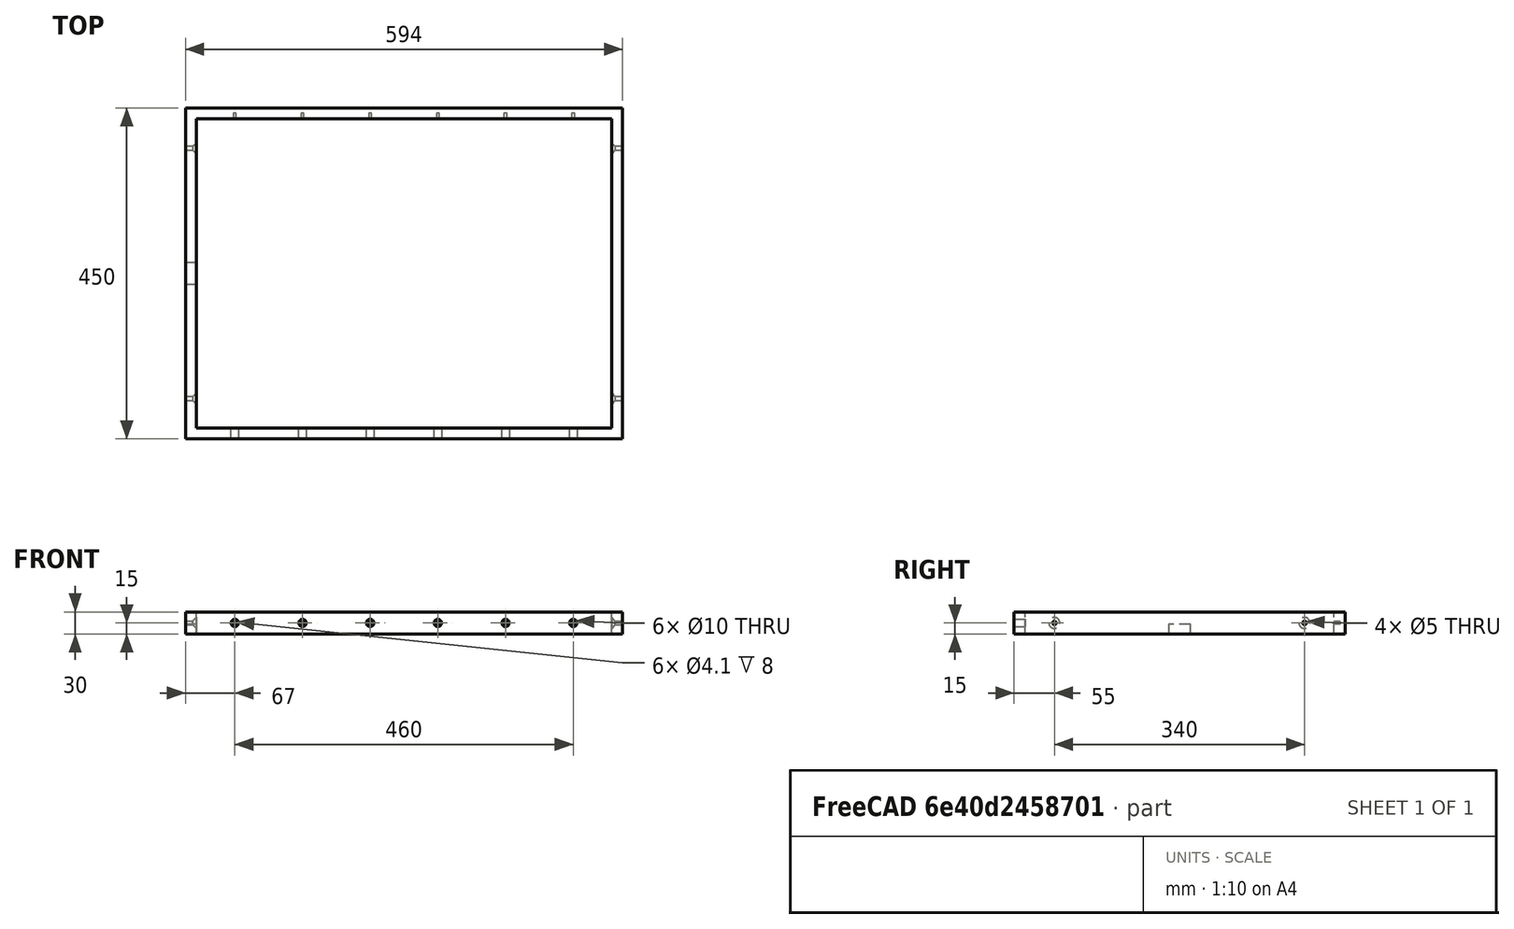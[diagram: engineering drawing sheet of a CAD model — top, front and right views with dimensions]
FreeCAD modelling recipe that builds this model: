
FCSTD DOCUMENT  (FreeCAD 1.0R39319 (Git))
Label: 02_frame_15_x_30
License: All rights reserved
LicenseURL: http://en.wikipedia.org/wiki/All_rights_reserved
objects: TechDraw::DrawViewDimension×20, TechDraw::DrawViewBalloon×9, Sketcher::SketchObject×5, TechDraw::DrawProjGroupItem×5, PartDesign::Pocket×4, TechDraw::DrawViewAnnotation×2, Spreadsheet::Sheet×1, PartDesign::Pad×1, PartDesign::Chamfer×1, PartDesign::Body×1, TechDraw::DrawSVGTemplate×1, TechDraw::DrawProjGroup×1, TechDraw::DrawPage×1
note: 59 computed .brp shape members not serialized (recipe doc carries the construction recipe); baked Part::Feature solids carry a one-line shape summary decoded from their .brp

FEATURE [Sketcher::SketchObject] Sketch
  ArcFitTolerance = 1e-06
  AttachmentSupport = -> [XY_Plane]
  FullyConstrained = true
  MakeInternals = false
  MapMode = 5
  expr: Constraints[22] = Spreadsheet.height_outside
  expr: Constraints[23] = Spreadsheet.lenght_outside
  expr: Constraints[24] = Spreadsheet.lenght_outside - 2 * Spreadsheet.height_frame
  expr: Constraints[25] = Spreadsheet.height_outside - 2 * Spreadsheet.height_frame
  sketch-geometry (10):
    g0: LineSegment StartX=-282 StartY=210 StartZ=0 EndX=-282 EndY=-210 EndZ=0
    g1: LineSegment StartX=-282 StartY=-210 StartZ=0 EndX=282 EndY=-210 EndZ=0
    g2: LineSegment StartX=282 StartY=-210 StartZ=0 EndX=282 EndY=210 EndZ=0
    g3: LineSegment StartX=282 StartY=210 StartZ=0 EndX=-282 EndY=210 EndZ=0
    g4: LineSegment [constr] StartX=-282 StartY=210 StartZ=0 EndX=282 EndY=-210 EndZ=0
    g5: LineSegment StartX=-297 StartY=225 StartZ=0 EndX=-297 EndY=-225 EndZ=0
    g6: LineSegment StartX=-297 StartY=-225 StartZ=0 EndX=297 EndY=-225 EndZ=0
    g7: LineSegment StartX=297 StartY=-225 StartZ=0 EndX=297 EndY=225 EndZ=0
    g8: LineSegment StartX=297 StartY=225 StartZ=0 EndX=-297 EndY=225 EndZ=0
    g9: LineSegment [constr] StartX=-297 StartY=225 StartZ=0 EndX=297 EndY=-225 EndZ=0
  constraints (26):
    c: Coincident(g0,g1)
    c: Coincident(g1,g2)
    c: Coincident(g2,g3)
    c: Coincident(g3,g0)
    c: Vertical(g0)
    c: Vertical(g2)
    c: Horizontal(g1)
    c: Horizontal(g3)
    c: Coincident(g4,g0)
    c: Coincident(g4,g1)
    c: Symmetric(g0,g1,g-1)
    c: Coincident(g5,g6)
    c: Coincident(g6,g7)
    c: Coincident(g7,g8)
    c: Coincident(g8,g5)
    c: Vertical(g5)
    c: Vertical(g7)
    c: Horizontal(g6)
    c: Horizontal(g8)
    c: Coincident(g9,g5)
    c: Coincident(g9,g6)
    c: Symmetric(g5,g6,g-1)
    c: DistanceY(g5,g5) = 450
    c: DistanceX(g8,g8) = 594
    c: DistanceX(g3,g3) = 564
    c: DistanceY(g0,g0) = 420
FEATURE [Spreadsheet::Sheet] Spreadsheet
  cells = A2='lenght_outside; B2(lenght_outside)=594; A3='height_outside; B3(height_outside)=450; A5='width_frame; B5(width_frame)=30; A6='height_frame; B6(height_frame)=15; A7='drill_size; B7(drillsize)=81
FEATURE [PartDesign::Pad] Pad
  Direction = (0,0,1)
  Length = 30
  Length2 = 10
  Profile = -> Sketch
  ReferenceAxis = -> Sketch [N_Axis]
  Suppressed = false
  Type = 0
  expr: Length = Spreadsheet.width_frame
FEATURE [Sketcher::SketchObject] Sketch001
  ArcFitTolerance = 1e-06
  AttachmentSupport = -> [YZ_Plane]
  FullyConstrained = true
  MakeInternals = false
  MapMode = 5
  Placement = pos=(0,0,0) rot=(0.57735,0.57735,0.57735;2.0944rad)
  sketch-geometry (4):
    g0: LineSegment StartX=-15 StartY=13 StartZ=0 EndX=-15 EndY=0 EndZ=0
    g1: LineSegment StartX=-15 StartY=0 StartZ=0 EndX=15 EndY=0 EndZ=0
    g2: LineSegment StartX=15 StartY=0 StartZ=0 EndX=15 EndY=13 EndZ=0
    g3: LineSegment StartX=15 StartY=13 StartZ=0 EndX=-15 EndY=13 EndZ=0
  constraints (11):
    c: Coincident(g0,g1)
    c: Coincident(g1,g2)
    c: Coincident(g2,g3)
    c: Coincident(g3,g0)
    c: Vertical(g0)
    c: Vertical(g2)
    c: Horizontal(g1)
    c: Symmetric(g0,g2,g-2)
    c: Horizontal(g1,g-1)
    c: DistanceX(g3,g3) = 30
    c: DistanceY(g0,g0) = 13
FEATURE [PartDesign::Pocket] Pocket
  BaseFeature = -> Pad
  Direction = (-1,0,0)
  Length = 594
  Length2 = 5
  Profile = -> Sketch001
  ReferenceAxis = -> Sketch001 [N_Axis]
  Suppressed = false
  Type = 0
  expr: Length = Spreadsheet.lenght_outside
FEATURE [Sketcher::SketchObject] Sketch002
  ArcFitTolerance = 1e-06
  AttachmentSupport = -> [XZ_Plane]
  ExternalGeometry = -> [Pocket]
  FullyConstrained = true
  MakeInternals = false
  MapMode = 5
  Placement = pos=(0,0,0) rot=(1,0,0;1.5708rad)
  sketch-geometry (7):
    g0: LineSegment [constr] StartX=-282 StartY=15 StartZ=0 EndX=282 EndY=15 EndZ=0
    g1: Circle CenterX=-230 CenterY=15 CenterZ=0 NormalX=0 NormalY=0 NormalZ=1 AngleXU=0 Radius=5
    g2: Circle CenterX=-138 CenterY=15 CenterZ=0 NormalX=0 NormalY=0 NormalZ=1 AngleXU=0 Radius=5
    g3: Circle CenterX=-46 CenterY=15 CenterZ=0 NormalX=0 NormalY=0 NormalZ=1 AngleXU=0 Radius=5
    g4: Circle CenterX=46 CenterY=15 CenterZ=0 NormalX=0 NormalY=0 NormalZ=1 AngleXU=0 Radius=5
    g5: Circle CenterX=138 CenterY=15 CenterZ=0 NormalX=0 NormalY=0 NormalZ=1 AngleXU=0 Radius=5
    g6: Circle CenterX=230 CenterY=15 CenterZ=0 NormalX=0 NormalY=0 NormalZ=1 AngleXU=0 Radius=5
  constraints (23):
    c: Symmetric(g-5,g-5,g0)
    c: Symmetric(g-6,g-6,g0)
    c: DistanceX(g-3,g-3) = 564
    c: PointOnObject(g1,g0)
    c: Diameter(g1) = 10
    c: PointOnObject(g2,g0)
    c: PointOnObject(g3,g0)
    c: PointOnObject(g4,g0)
    c: PointOnObject(g5,g0)
    c: Equal(g1,g2)
    c: Equal(g1,g3)
    c: Equal(g1,g4)
    c: Equal(g5,g1)
    c: PointOnObject(g6,g0)
    c: Equal(g1,g6)
    c: DistanceX(g0,g1) = 52
    c: DistanceX(g6,g0) = 52
    c: DistanceX(g1,g6) = 460
    c: DistanceX(g1,g2) = 92
    c: DistanceX(g2,g3) = 92
    c: DistanceX(g3,g4) = 92
    c: DistanceX(g4,g5) = 92
    c: DistanceX(g5,g6) = 92
FEATURE [PartDesign::Pocket] Pocket001
  BaseFeature = -> Pocket
  Direction = (0,1,-2e-16)
  Length = 225
  Length2 = 5
  Profile = -> Sketch002
  ReferenceAxis = -> Sketch002 [N_Axis]
  Reversed = true
  Suppressed = false
  Type = 0
  expr: Length = Spreadsheet.height_outside / 2
FEATURE [Sketcher::SketchObject] Sketch003
  ArcFitTolerance = 1e-06
  AttachmentSupport = -> [XZ_Plane]
  ExternalGeometry = -> [Pocket001]
  FullyConstrained = true
  MakeInternals = false
  MapMode = 5
  Placement = pos=(0,0,0) rot=(1,0,0;1.5708rad)
  sketch-geometry (7):
    g0: LineSegment [constr] StartX=-282 StartY=15 StartZ=0 EndX=282 EndY=15 EndZ=0
    g1: Circle CenterX=-230 CenterY=15 CenterZ=0 NormalX=0 NormalY=0 NormalZ=1 AngleXU=0 Radius=2.05
    g2: Circle CenterX=-138 CenterY=15 CenterZ=0 NormalX=0 NormalY=0 NormalZ=1 AngleXU=0 Radius=2.05
    g3: Circle CenterX=-46 CenterY=15 CenterZ=0 NormalX=0 NormalY=0 NormalZ=1 AngleXU=0 Radius=2.05
    g4: Circle CenterX=46 CenterY=15 CenterZ=0 NormalX=0 NormalY=0 NormalZ=1 AngleXU=0 Radius=2.05
    g5: Circle CenterX=138 CenterY=15 CenterZ=0 NormalX=0 NormalY=0 NormalZ=1 AngleXU=0 Radius=2.05
    g6: Circle CenterX=230 CenterY=15 CenterZ=0 NormalX=0 NormalY=0 NormalZ=1 AngleXU=0 Radius=2.05
  constraints (22):
    c: Horizontal(g0)
    c: PointOnObject(g0,g-4)
    c: Symmetric(g-3,g-3,g0)
    c: PointOnObject(g1,g0)
    c: Distance(g1,g-3) = 52
    c: Diameter(g1) = 4.1
    c: PointOnObject(g2,g0)
    c: DistanceX(g1,g2) = 92
    c: Equal(g1,g2)
    c: PointOnObject(g3,g0)
    c: Equal(g2,g3)
    c: PointOnObject(g4,g0)
    c: PointOnObject(g5,g0)
    c: Equal(g1,g4)
    c: Equal(g1,g5)
    c: DistanceX(g2,g3) = 92
    c: DistanceX(g3,g4) = 92
    c: DistanceX(g4,g5) = 92
    c: PointOnObject(g6,g0)
    c: Equal(g1,g6)
    c: DistanceX(g5,g6) = 92
    c: DistanceX(g6,g0) = 52
FEATURE [PartDesign::Pocket] Pocket002
  BaseFeature = -> Pocket001
  Direction = (0,1,-2e-16)
  Length = 218
  Length2 = 5
  Profile = -> Sketch003
  ReferenceAxis = -> Sketch003 [N_Axis]
  Suppressed = false
  Type = 0
  expr: Length = Spreadsheet.height_outside / 2 - 7
FEATURE [Sketcher::SketchObject] Sketch004
  ArcFitTolerance = 1e-06
  AttachmentSupport = -> [YZ_Plane]
  ExternalGeometry = -> [Pocket002]
  FullyConstrained = true
  MakeInternals = false
  MapMode = 5
  Placement = pos=(0,0,0) rot=(0.57735,0.57735,0.57735;2.0944rad)
  sketch-geometry (3):
    g0: LineSegment [constr] StartX=-210 StartY=15 StartZ=0 EndX=210 EndY=15 EndZ=0
    g1: Circle CenterX=-170 CenterY=15 CenterZ=0 NormalX=0 NormalY=0 NormalZ=1 AngleXU=0 Radius=2.5
    g2: Circle CenterX=170 CenterY=15 CenterZ=0 NormalX=0 NormalY=0 NormalZ=1 AngleXU=0 Radius=2.5
  constraints (8):
    c: Symmetric(g-3,g-3,g0)
    c: Symmetric(g-4,g-4,g0)
    c: PointOnObject(g1,g0)
    c: PointOnObject(g2,g0)
    c: Distance(g1,g-3) = 40
    c: Distance(g0,g2) = 40
    c: Diameter(g1) = 5
    c: Equal(g1,g2)
FEATURE [PartDesign::Pocket] Pocket003
  BaseFeature = -> Pocket002
  Direction = (-1,0,0)
  Length = 5
  Length2 = 5
  Midplane = true
  Profile = -> Sketch004
  ReferenceAxis = -> Sketch004 [N_Axis]
  Suppressed = false
  Type = 1
FEATURE [PartDesign::Chamfer] Chamfer
  Angle = 45
  Base = -> Pocket003 [Edge41,Edge43,Edge57,Edge58]
  BaseFeature = -> Pocket003
  ChamferType = 0
  FlipDirection = false
  Size = 5
  Size2 = 1
  SupportTransform = false
  Suppressed = false
  UseAllEdges = false
FEATURE [PartDesign::Body] Body
  AllowCompound = false
  Group = -> [Sketch,Pad,Sketch001,Pocket,Sketch002,Pocket001,Sketch003,Pocket002,Sketch004,Pocket003,Chamfer]
  Origin = -> Origin
  Tip = -> Chamfer
FEATURE [TechDraw::DrawSVGTemplate] Template
  EditableTexts = AuthorName=Matthias Mosimann; CheckDate=N/A; CreationDate=15/04/2026; DrawingNumber=1.0; FC-Title=Rahmen; SheetNumber=1 / 1; SupervisorName=N/A; Weight=WEIGHT; scale=1 : 5
  Height = 297
  Orientation = 1
  Template = C:/Program Files/FreeCAD 1.0/data/Mod/TechDraw/Templates/A3_Landscape_TD.svg
  Width = 420
FEATURE [TechDraw::DrawProjGroupItem] View  label="Front"
  CoarseView = false
  Direction = (0,-1,0)
  Focus = 100
  HardHidden = false
  IsoCount = 0
  IsoHidden = false
  IsoVisible = false
  LockPosition = true
  Perspective = false
  Rotation = 0
  RotationVector = (1,0,0)
  Scale = 0.2
  ScaleType = 2
  ScrubCount = 1
  SeamHidden = false
  SeamVisible = true
  SmoothHidden = false
  SmoothVisible = true
  Source = -> [Body]
  Type = 0
  X = 0
  XDirection = (-1,0,-1e-16)
  Y = 0
FEATURE [TechDraw::DrawProjGroupItem] ProjItem  label="Right"
  CoarseView = false
  Direction = (-1,-1e-16,-1e-16)
  Focus = 100
  HardHidden = false
  IsoCount = 0
  IsoHidden = false
  IsoVisible = false
  LockPosition = true
  Perspective = false
  Rotation = 0
  RotationVector = (1,0,0)
  Scale = 0.2
  ScaleType = 2
  ScrubCount = 1
  SeamHidden = false
  SeamVisible = true
  SmoothHidden = false
  SmoothVisible = true
  Source = -> [Body]
  Type = 2
  X = -119.062
  XDirection = (-1e-16,1,0)
  Y = 0
FEATURE [TechDraw::DrawProjGroupItem] ProjItem002  label="Top"
  CoarseView = false
  Direction = (1e-16,0,-1)
  Focus = 100
  HardHidden = true
  IsoCount = 0
  IsoHidden = false
  IsoVisible = false
  LockPosition = true
  Perspective = false
  Rotation = 0
  RotationVector = (1,0,0)
  Scale = 0.2
  ScaleType = 2
  ScrubCount = 1
  SeamHidden = false
  SeamVisible = true
  SmoothHidden = false
  SmoothVisible = true
  Source = -> [Body]
  Type = 4
  X = 0
  XDirection = (-1,0,-1e-16)
  Y = -80.6268
FEATURE [TechDraw::DrawProjGroupItem] ProjItem003  label="Left"
  CoarseView = false
  Direction = (1,-1e-16,1e-16)
  Focus = 100
  HardHidden = false
  IsoCount = 0
  IsoHidden = false
  IsoVisible = false
  LockPosition = true
  Perspective = false
  Rotation = 0
  RotationVector = (1,0,0)
  Scale = 0.2
  ScaleType = 2
  ScrubCount = 1
  SeamHidden = false
  SeamVisible = true
  SmoothHidden = false
  SmoothVisible = true
  Source = -> [Body]
  Type = 1
  X = 121.888
  XDirection = (-1e-16,-1,0)
  Y = 0
FEATURE [TechDraw::DrawProjGroupItem] ProjItem004  label="FrontTopLeft"
  CoarseView = false
  Direction = (0.57735,-0.57735,-0.57735)
  Focus = 100
  HardHidden = false
  IsoCount = 0
  IsoHidden = false
  IsoVisible = false
  LockPosition = true
  Perspective = false
  Rotation = 0
  RotationVector = (1,0,0)
  Scale = 0.2
  ScaleType = 2
  ScrubCount = 1
  SeamHidden = false
  SeamVisible = true
  SmoothHidden = false
  SmoothVisible = true
  Source = -> [Body]
  Type = 6
  X = 147.596
  XDirection = (-0.707107,-0.707107,-1e-16)
  Y = -76.8368
FEATURE [TechDraw::DrawProjGroup] ProjGroup
  Anchor = -> View
  AutoDistribute = true
  LockPosition = false
  ProjectionType = 0
  Rotation = 0
  Scale = 0.2
  ScaleType = 2
  Source = -> [Body]
  Views = -> [View,ProjItem,ProjItem002,ProjItem003,ProjItem004]
  X = 185.522
  Y = 222.445
  spacingX = 15
  spacingY = 15
FEATURE [TechDraw::DrawViewDimension] Dimension
  AngleOverride = false
  Arbitrary = false
  ArbitraryTolerances = false
  BoxCorners = (2) [(-59.4,-45,0),(59.4,45,0)]
  EqualTolerance = true
  ExtensionAngle = 0
  FormatSpec = %.2w
  FormatSpecOverTolerance = %+.2w
  FormatSpecUnderTolerance = %+.2w
  Inverted = false
  LineAngle = 0
  LockPosition = false
  MeasureType = 1
  OverTolerance = 0
  References2D = -> [ProjItem002]
  Rotation = 0
  ScaleType = 0
  TheoreticalExact = false
  Type = 2
  UnderTolerance = 0
  X = -72.114
  Y = 5.93997
FEATURE [TechDraw::DrawViewDimension] Dimension001
  AngleOverride = false
  Arbitrary = false
  ArbitraryTolerances = false
  BoxCorners = (2) [(-59.4,-45,0),(59.4,45,0)]
  EqualTolerance = true
  ExtensionAngle = 0
  FormatSpec = %.2w
  FormatSpecOverTolerance = %+.2w
  FormatSpecUnderTolerance = %+.2w
  Inverted = false
  LineAngle = 0
  LockPosition = false
  MeasureType = 1
  OverTolerance = 0
  References2D = -> [ProjItem002]
  Rotation = 0
  ScaleType = 0
  TheoreticalExact = false
  Type = 1
  UnderTolerance = 0
  X = 0
  Y = 61.892
FEATURE [TechDraw::DrawViewDimension] Dimension002
  AngleOverride = false
  Arbitrary = false
  ArbitraryTolerances = false
  BoxCorners = (2) [(-45,-3,0),(45,3,0)]
  EqualTolerance = true
  ExtensionAngle = 0
  FormatSpec = %.2w
  FormatSpecOverTolerance = %+.2w
  FormatSpecUnderTolerance = %+.2w
  Inverted = false
  LineAngle = 0
  LockPosition = false
  MeasureType = 1
  OverTolerance = 0
  References2D = -> [ProjItem]
  Rotation = 0
  ScaleType = 0
  TheoreticalExact = false
  Type = 0
  UnderTolerance = 0
  X = -39.5
  Y = -15.8335
FEATURE [TechDraw::DrawViewDimension] Dimension003
  AngleOverride = false
  Arbitrary = false
  ArbitraryTolerances = false
  BoxCorners = (2) [(-45,-3,0),(45,3,0)]
  EqualTolerance = true
  ExtensionAngle = 0
  FormatSpec = ⌀%.2w
  FormatSpecOverTolerance = %+.2w
  FormatSpecUnderTolerance = %+.2w
  Inverted = false
  LineAngle = 0
  LockPosition = false
  MeasureType = 1
  OverTolerance = 0
  References2D = -> [ProjItem]
  Rotation = 0
  ScaleType = 0
  TheoreticalExact = false
  Type = 5
  UnderTolerance = 0
  X = -30.7122
  Y = 14.8466
FEATURE [TechDraw::DrawViewDimension] Dimension004
  AngleOverride = false
  Arbitrary = false
  ArbitraryTolerances = false
  BoxCorners = (2) [(-45,-3,0),(45,3,0)]
  EqualTolerance = true
  ExtensionAngle = 0
  FormatSpec = %.2w
  FormatSpecOverTolerance = %+.2w
  FormatSpecUnderTolerance = %+.2w
  Inverted = false
  LineAngle = 0
  LockPosition = false
  MeasureType = 1
  OverTolerance = 0
  References2D = -> [ProjItem]
  Rotation = 0
  ScaleType = 0
  TheoreticalExact = false
  Type = 0
  UnderTolerance = 0
  X = 39.5
  Y = -15.8335
FEATURE [TechDraw::DrawViewDimension] Dimension005
  AngleOverride = false
  Arbitrary = false
  ArbitraryTolerances = false
  BoxCorners = (2) [(-45,-3,0),(45,3,0)]
  EqualTolerance = true
  ExtensionAngle = 0
  FormatSpec = ⌀%.2w
  FormatSpecOverTolerance = %+.2w
  FormatSpecUnderTolerance = %+.2w
  Inverted = false
  LineAngle = 0
  LockPosition = false
  MeasureType = 1
  OverTolerance = 0
  References2D = -> [ProjItem]
  Rotation = 0
  ScaleType = 0
  TheoreticalExact = false
  Type = 5
  UnderTolerance = 0
  X = 38.1595
  Y = 15.5364
FEATURE [TechDraw::DrawViewDimension] Dimension006
  AngleOverride = false
  Arbitrary = false
  ArbitraryTolerances = false
  BoxCorners = (2) [(-45,-3,0),(45,3,0)]
  EqualTolerance = true
  ExtensionAngle = 0
  FormatSpec = %.2w
  FormatSpecOverTolerance = %+.2w
  FormatSpecUnderTolerance = %+.2w
  Inverted = false
  LineAngle = 0
  LockPosition = false
  MeasureType = 1
  OverTolerance = 0
  References2D = -> [ProjItem]
  Rotation = 0
  ScaleType = 0
  TheoreticalExact = false
  Type = 0
  UnderTolerance = 0
  X = -13.9563
  Y = 10.1442
FEATURE [TechDraw::DrawViewDimension] Dimension007
  AngleOverride = false
  Arbitrary = false
  ArbitraryTolerances = false
  BoxCorners = (2) [(-45,-3,0),(45,3,0)]
  EqualTolerance = true
  ExtensionAngle = 0
  FormatSpec = %.2w
  FormatSpecOverTolerance = %+.2w
  FormatSpecUnderTolerance = %+.2w
  Inverted = false
  LineAngle = 0
  LockPosition = false
  MeasureType = 1
  OverTolerance = 0
  References2D = -> [ProjItem]
  Rotation = 0
  ScaleType = 0
  TheoreticalExact = false
  Type = 0
  UnderTolerance = 0
  X = -17.7771
  Y = 24.7768
FEATURE [TechDraw::DrawViewDimension] Dimension008
  AngleOverride = false
  Arbitrary = false
  ArbitraryTolerances = false
  BoxCorners = (2) [(-59.4,-3,0),(59.4,3,0)]
  EqualTolerance = true
  ExtensionAngle = 0
  FormatSpec = %.2w
  FormatSpecOverTolerance = %+.2w
  FormatSpecUnderTolerance = %+.2w
  Inverted = false
  LineAngle = 0
  LockPosition = false
  MeasureType = 1
  OverTolerance = 0
  References2D = -> [View]
  Rotation = 0
  ScaleType = 0
  TheoreticalExact = false
  Type = 0
  UnderTolerance = 0
  X = -52.7
  Y = 22.4873
FEATURE [TechDraw::DrawViewDimension] Dimension009
  AngleOverride = false
  Arbitrary = false
  ArbitraryTolerances = false
  BoxCorners = (2) [(-59.4,-3,0),(59.4,3,0)]
  EqualTolerance = true
  ExtensionAngle = 0
  FormatSpec = %.2w
  FormatSpecOverTolerance = %+.2w
  FormatSpecUnderTolerance = %+.2w
  Inverted = false
  LineAngle = 0
  LockPosition = false
  MeasureType = 1
  OverTolerance = 0
  References2D = -> [View]
  Rotation = 0
  ScaleType = 0
  TheoreticalExact = false
  Type = 1
  UnderTolerance = 0
  X = -36.8
  Y = 22.4873
FEATURE [TechDraw::DrawViewDimension] Dimension010
  AngleOverride = false
  Arbitrary = false
  ArbitraryTolerances = false
  BoxCorners = (2) [(-59.4,-3,0),(59.4,3,0)]
  EqualTolerance = true
  ExtensionAngle = 0
  FormatSpec = %.2w
  FormatSpecOverTolerance = %+.2w
  FormatSpecUnderTolerance = %+.2w
  Inverted = false
  LineAngle = 0
  LockPosition = false
  MeasureType = 1
  OverTolerance = 0
  References2D = -> [View]
  Rotation = 0
  ScaleType = 0
  TheoreticalExact = false
  Type = 2
  UnderTolerance = 0
  X = 65.2162
  Y = 0
FEATURE [TechDraw::DrawViewDimension] Dimension011
  AngleOverride = false
  Arbitrary = false
  ArbitraryTolerances = false
  BoxCorners = (2) [(-59.4,-45,0),(59.4,45,0)]
  EqualTolerance = true
  ExtensionAngle = 0
  FormatSpec = %.2w
  FormatSpecOverTolerance = %+.2w
  FormatSpecUnderTolerance = %+.2w
  Inverted = false
  LineAngle = 0
  LockPosition = false
  MeasureType = 1
  OverTolerance = 0
  References2D = -> [ProjItem002]
  Rotation = 0
  ScaleType = 0
  TheoreticalExact = false
  Type = 0
  UnderTolerance = 0
  X = 62.2692
  Y = 54.4773
FEATURE [TechDraw::DrawViewDimension] Dimension012
  AngleOverride = false
  Arbitrary = false
  ArbitraryTolerances = false
  BoxCorners = (2) [(-59.4,-3,0),(59.4,3,0)]
  EqualTolerance = true
  ExtensionAngle = 0
  FormatSpec = %.2w
  FormatSpecOverTolerance = %+.2w
  FormatSpecUnderTolerance = %+.2w
  Inverted = false
  LineAngle = 0
  LockPosition = false
  MeasureType = 1
  OverTolerance = 0
  References2D = -> [View]
  Rotation = 0
  ScaleType = 0
  TheoreticalExact = false
  Type = 1
  UnderTolerance = 0
  X = -18.4
  Y = 22.4873
FEATURE [TechDraw::DrawViewDimension] Dimension013
  AngleOverride = false
  Arbitrary = false
  ArbitraryTolerances = false
  BoxCorners = (2) [(-59.4,-3,0),(59.4,3,0)]
  EqualTolerance = true
  ExtensionAngle = 0
  FormatSpec = %.2w
  FormatSpecOverTolerance = %+.2w
  FormatSpecUnderTolerance = %+.2w
  Inverted = false
  LineAngle = 0
  LockPosition = false
  MeasureType = 1
  OverTolerance = 0
  References2D = -> [View]
  Rotation = 0
  ScaleType = 0
  TheoreticalExact = false
  Type = 1
  UnderTolerance = 0
  X = 0
  Y = 22.4873
FEATURE [TechDraw::DrawViewDimension] Dimension014
  AngleOverride = false
  Arbitrary = false
  ArbitraryTolerances = false
  BoxCorners = (2) [(-59.4,-3,0),(59.4,3,0)]
  EqualTolerance = true
  ExtensionAngle = 0
  FormatSpec = %.2w
  FormatSpecOverTolerance = %+.2w
  FormatSpecUnderTolerance = %+.2w
  Inverted = false
  LineAngle = 0
  LockPosition = false
  MeasureType = 1
  OverTolerance = 0
  References2D = -> [View]
  Rotation = 0
  ScaleType = 0
  TheoreticalExact = false
  Type = 1
  UnderTolerance = 0
  X = 18.4
  Y = 22.4873
FEATURE [TechDraw::DrawViewDimension] Dimension015
  AngleOverride = false
  Arbitrary = false
  ArbitraryTolerances = false
  BoxCorners = (2) [(-59.4,-3,0),(59.4,3,0)]
  EqualTolerance = true
  ExtensionAngle = 0
  FormatSpec = %.2w
  FormatSpecOverTolerance = %+.2w
  FormatSpecUnderTolerance = %+.2w
  Inverted = false
  LineAngle = 0
  LockPosition = false
  MeasureType = 1
  OverTolerance = 0
  References2D = -> [View]
  Rotation = 0
  ScaleType = 0
  TheoreticalExact = false
  Type = 1
  UnderTolerance = 0
  X = 36.8
  Y = 22.4873
FEATURE [TechDraw::DrawViewDimension] Dimension016
  AngleOverride = false
  Arbitrary = false
  ArbitraryTolerances = false
  BoxCorners = (2) [(-59.4,-3,0),(59.4,3,0)]
  EqualTolerance = true
  ExtensionAngle = 0
  FormatSpec = %.2w
  FormatSpecOverTolerance = %+.2w
  FormatSpecUnderTolerance = %+.2w
  Inverted = false
  LineAngle = 0
  LockPosition = false
  MeasureType = 1
  OverTolerance = 0
  References2D = -> [View]
  Rotation = 0
  ScaleType = 0
  TheoreticalExact = false
  Type = 0
  UnderTolerance = 0
  X = 52.7
  Y = 22.4873
FEATURE [TechDraw::DrawViewAnnotation] Annotation005
  Font = osifont
  LineSpace = 80
  LockPosition = false
  MaxWidth = 100
  Rotation = 0
  Scale = 0.5
  ScaleType = 1
  Text = Rahmen ist aus Flachstahl 30mm x 15mm. | 3D Ansichten können von der angegebenen Skalierungsgrösse abweichen. | Alle Angaben in mm.
  TextSize = 3
  TextStyle = 1
  X = 65.8486
  Y = 170.219
FEATURE [TechDraw::DrawViewBalloon] Balloon
  BubbleShape = 0
  EndType = 0
  EndTypeScale = 1
  KinkLength = 5
  LockPosition = false
  OriginX = -67.1399
  OriginY = 96.7687
  Rotation = 0
  ScaleType = 0
  ShapeScale = 1
  SourceView = -> Annotation005
  Text = 1
  TextWrapLen = -1
  X = -98.1022
  Y = 165.989
FEATURE [TechDraw::DrawViewAnnotation] Annotation
  Font = osifont
  LineSpace = 80
  LockPosition = false
  MaxWidth = 100
  Rotation = 0
  Scale = 0.5
  ScaleType = 1
  Text = (1) Montageloch kann frei gewählt werden im Durchmesser und Platzierung. Wichtig ist dass auf der Innenseite Senkungen passend vorhanden sind. Hier sind nur Beispiele eingezeichnet.   | (2) Unten im Rahmen werden die Edelstahlhülsen mit Sackloch eingeschweist. Bohrung muss ggf. etwas grösser sein als 10mm, damit die Hülse passt. | (3) Oben im Rahmen werden nur die 4.1mm Sacklöcher gebohrt. Ohne Hülsen.
  TextSize = 3
  TextStyle = 0
  X = 65.8486
  Y = 113.793
FEATURE [TechDraw::DrawViewBalloon] Balloon002
  BubbleShape = 0
  EndType = 0
  EndTypeScale = 1
  KinkLength = 5
  LockPosition = false
  OriginX = -225
  OriginY = 0
  Rotation = 0
  ScaleType = 0
  ShapeScale = 1
  SourceView = -> View
  Text = 2
  TextWrapLen = -1
  X = -121.803
  Y = -73.4565
FEATURE [TechDraw::DrawViewBalloon] Balloon003
  BubbleShape = 0
  EndType = 0
  EndTypeScale = 1
  KinkLength = 5
  LockPosition = false
  OriginX = -5.29303
  OriginY = -183.225
  Rotation = 0
  ScaleType = 0
  ShapeScale = 1
  SourceView = -> ProjItem004
  Text = 2
  TextWrapLen = -1
  X = 166.509
  Y = -226.829
FEATURE [TechDraw::DrawViewBalloon] Balloon004
  BubbleShape = 0
  EndType = 0
  EndTypeScale = 1
  KinkLength = 5
  LockPosition = false
  OriginX = -135.95
  OriginY = 0
  Rotation = 0
  ScaleType = 0
  ShapeScale = 1
  SourceView = -> View
  Text = 3
  TextWrapLen = -1
  X = -243.989
  Y = 155.417
FEATURE [TechDraw::DrawViewBalloon] Balloon005
  BubbleShape = 0
  EndType = 0
  EndTypeScale = 1
  KinkLength = 5
  LockPosition = false
  OriginX = -116.686
  OriginY = 105.548
  Rotation = 0
  ScaleType = 0
  ShapeScale = 1
  SourceView = -> ProjItem004
  Text = 3
  TextWrapLen = -1
  X = -266.453
  Y = 203.449
FEATURE [TechDraw::DrawViewBalloon] Balloon006
  BubbleShape = 0
  EndType = 0
  EndTypeScale = 1
  KinkLength = 5
  LockPosition = false
  OriginX = 75.446
  OriginY = 191.023
  Rotation = 0
  ScaleType = 0
  ShapeScale = 1
  SourceView = -> ProjItem004
  Text = 1
  TextWrapLen = -1
  X = 175.446
  Y = 291.023
FEATURE [TechDraw::DrawViewDimension] Dimension017
  AngleOverride = false
  Arbitrary = false
  ArbitraryTolerances = false
  BoxCorners = (2) [(-59.4,-3,0),(59.4,3,0)]
  EqualTolerance = true
  ExtensionAngle = 0
  FormatSpec = ⌀%.2w
  FormatSpecOverTolerance = %+.2w
  FormatSpecUnderTolerance = %+.2w
  Inverted = false
  LineAngle = 0
  LockPosition = false
  MeasureType = 1
  OverTolerance = 0
  References2D = -> [View]
  Rotation = 0
  ScaleType = 0
  TheoreticalExact = true
  Type = 5
  UnderTolerance = 0
  X = -66.349
  Y = -6.38909
FEATURE [TechDraw::DrawViewDimension] Dimension018
  AngleOverride = false
  Arbitrary = false
  ArbitraryTolerances = false
  BoxCorners = (2) [(-59.4,-3,0),(59.4,3,0)]
  EqualTolerance = true
  ExtensionAngle = 0
  FormatSpec = ⌀%.2w
  FormatSpecOverTolerance = %+.2w
  FormatSpecUnderTolerance = %+.2w
  Inverted = false
  LineAngle = 0
  LockPosition = false
  MeasureType = 1
  OverTolerance = 0
  References2D = -> [View]
  Rotation = 0
  ScaleType = 0
  TheoreticalExact = false
  Type = 5
  UnderTolerance = 0
  X = -66.044
  Y = 23.5898
FEATURE [TechDraw::DrawViewDimension] Dimension019
  AngleOverride = false
  Arbitrary = false
  ArbitraryTolerances = false
  BoxCorners = (2) [(-59.4,-45,-1e-07),(59.4,45,1e-07)]
  EqualTolerance = true
  ExtensionAngle = 0
  FormatSpec = %.2w
  FormatSpecOverTolerance = %+.2w
  FormatSpecUnderTolerance = %+.2w
  Inverted = false
  LineAngle = 0
  LockPosition = false
  MeasureType = 1
  OverTolerance = 0
  References2D = -> [ProjItem002]
  Rotation = 0
  ScaleType = 0
  TheoreticalExact = false
  Type = 0
  UnderTolerance = 0
  X = -42.8631
  Y = 50.9888
FEATURE [TechDraw::DrawViewBalloon] Balloon007
  BubbleShape = 0
  EndType = 0
  EndTypeScale = 1
  KinkLength = 5
  LockPosition = false
  OriginX = -232.05
  OriginY = 214
  Rotation = 0
  ScaleType = 0
  ShapeScale = 1
  SourceView = -> ProjItem002
  Text = 3
  TextWrapLen = -1
  X = -331.685
  Y = 266.2
FEATURE [TechDraw::DrawViewBalloon] Balloon008
  BubbleShape = 0
  EndType = 0
  EndTypeScale = 1
  KinkLength = 5
  LockPosition = false
  OriginX = -284.5
  OriginY = 175
  Rotation = 0
  ScaleType = 0
  ShapeScale = 1
  SourceView = -> ProjItem002
  Text = 1
  TextWrapLen = -1
  X = -390.448
  Y = 196.452
FEATURE [TechDraw::DrawViewBalloon] Balloon009
  BubbleShape = 0
  EndType = 0
  EndTypeScale = 1
  KinkLength = 5
  LockPosition = false
  OriginX = -143
  OriginY = -217.5
  Rotation = 0
  ScaleType = 0
  ShapeScale = 1
  SourceView = -> ProjItem002
  Text = 2
  TextWrapLen = -1
  X = -270.817
  Y = -305.468
FEATURE [TechDraw::DrawPage] Page
  KeepUpdated = true
  NextBalloonIndex = 11
  ProjectionType = 0
  Template = -> Template
  Views = -> [ProjGroup,Dimension,Dimension001,Dimension002,Dimension003,Dimension004,Dimension005,Dimension006,Dimension007,Dimension008,Dimension009,Dimension010,Dimension011,Dimension012,Dimension013,Dimension014,Dimension015,Dimension016,Annotation005,Balloon,Annotation,Balloon002,Balloon003,Balloon004,Balloon005,Balloon006,Dimension017,Dimension018,Dimension019,Balloon007,Balloon008,Balloon009]
